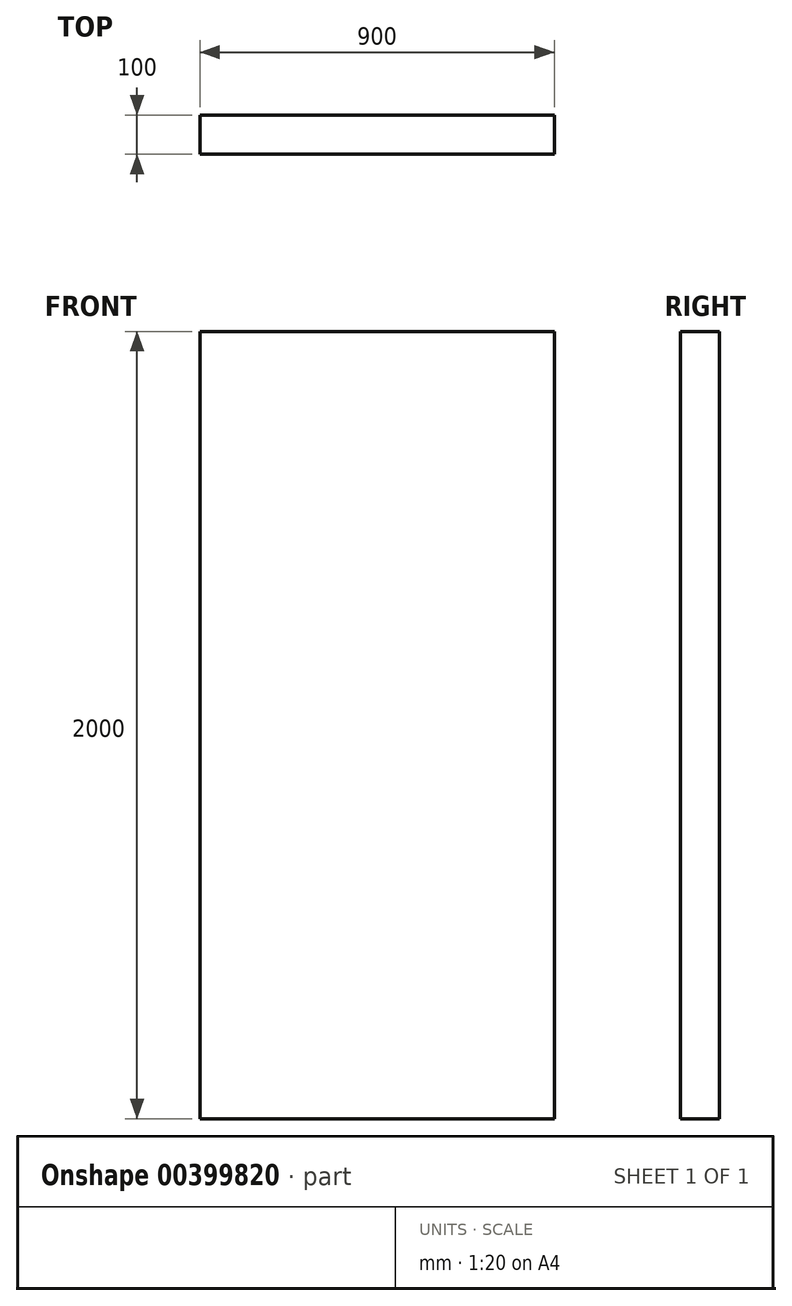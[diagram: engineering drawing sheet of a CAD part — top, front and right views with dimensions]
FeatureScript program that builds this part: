
annotation { "Feature Type Name" : "Feature", "Feature Type Description" : "" }
export const myFeature = defineFeature(function(context is Context, id is Id, definition is map)
    precondition{}
    {
        {
            var Q0;
            Q0=qCreatedBy(makeId("Top.planeOp"),FACE);
            var sketch = newSketch(context, id + "F0", { "sketchPlane" : qUnion([Q0])});
            skLineSegment(sketch, "E0.bottom", {"start": v(0, 0) * mm, "end": v(900, 0) * mm});
            skLineSegment(sketch, "E0.top", {"start": v(0, 100) * mm, "end": v(900, 100) * mm});
            skLineSegment(sketch, "E0.left", {"start": v(0, 0) * mm, "end": v(0, 100) * mm});
            skLineSegment(sketch, "E0.right", {"start": v(900, 0) * mm, "end": v(900, 100) * mm});
            skSolve(sketch);
        }
        {
            var Q0;
            Q0 = qSketchRegion(id + "F0", true);
            extrude(context, id + "F1", {"entities" : qUnion([Q0]), "depth" : 2000 * mm});
        }
    });
